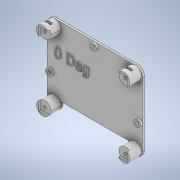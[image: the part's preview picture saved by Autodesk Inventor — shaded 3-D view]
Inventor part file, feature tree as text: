
AUTODESK INVENTOR PART (.ipt)
format: ipt  version: 2020.3 (Build 243373000, 373)  size: 1,038,336 bytes
history: native  units: mm
features: other x10, plane x8, sketch x8, extrude x6, projected_geometry x4, mirror x2, hole x1
ambient origin geometry x8: Origin, YZ Plane, XZ Plane, XY Plane, X Axis, Y Axis, Z Axis, Center Point
bodies: Volumenkörper2 (feature_tree), Volumenkörper1 (feature_tree)
feature tree (39):
  other  "Querschnitt1"
  other  "Querschnitt2"
  extrude  "Extrusion0"  Depth=31.5mm
  extrude  "Extrusion0.1"  Depth=31.5mm
  other  "Arbeitsachse1"
  plane  "Arbeitsebene1"
  sketch  "Skizze2.0"  dims[d0=2.0mm]
  plane  "Arbeitsebene7"
  sketch  "Skizze2.1"  dims[d9=3.5mm d10=31.5mm]
  other  "Arbeitspunkt1"
  other  "Arbeitsachse2"
  other  "Arbeitsachse3"
  plane  "Arbeitsebene2"
  sketch  "Skizze2.2"  dims[d16=3.2mm d17=3.2mm]
  extrude  "Extrusion2.0"  Depth=76.5mm
  plane  "Arbeitsebene4"
  plane  "Arbeitsebene5"
  hole  "Bohrung1"  [1 undecoded]
  extrude  "Extrusion2.1"  Depth=3.2mm
  extrude  "Extrusion6"  Depth=3.2mm
  plane  "Arbeitsebene3"
  extrude  "Extrusion2"  Depth=1.0mm
  mirror  "Spiegeln1"
  other  "Arbeitsachse4"
  other  "Arbeitsachse5"
  plane  "Arbeitsebene8"
  mirror  "Spiegeln2"
  other  "Prägen1"
  sketch  "Skizze1"  dims[d11=93.5mm d12=76.5mm]
  sketch  "Skizze3"  dims[d18=3.2mm d19=3.2mm]
  sketch  "Skizze4"  dims[d20=11.0mm d21=10.0mm d22=0.0mm d23=0.0mm d25=5.6mm d26=0.2mm d27=3.0mm d28=20.0mm d29=2.2mm d30=0.0mm d31=7.5mm d32=57.0mm d33=10.0mm d34=82.0mm d35=1.0mm d36=0.0mm d37=30.0mm d38=30.0mm d39=30.0mm d40=30.0mm d41=40.0mm d42=0.0mm d44=0.5mm d45=2.0mm d46=-33.0mm d47=20.0mm d50=75.2mm d51=90.2mm d52=7.0mm d53=12.0mm d54=0.0mm d55=2.0mm d58=13.0mm d59=13.0mm d60=10.0mm d61=0.0mm d62=82.0mm d63=67.0mm d72=82.0mm d73=67.0mm d75=82.0mm d76=2.0mm d77=0.0mm d78=14.0mm d81=0.0mm d82=67.0mm d83=0.5mm d84=2.0mm d85=40.75mm d86=20.0mm d87=6.5mm d89=67.0mm]
  sketch  "Skizze00"  dims[d1=4.0mm d2=6.0mm d3=4.0mm d4=2.0mm d5=90.0deg d6=8.0mm d7=20.594885mm d8=31.5mm]
  sketch  "Skizze01"  dims[d13=48.5mm d15=3.0mm]
  projected_geometry  "Projizierte Kontur4"
  projected_geometry  "Projizierte Kontur5"
  projected_geometry  "Projizierte Kontur6"
  projected_geometry  "Projizierte Kontur7"
  plane  "Arbeitsebene0"
  other  "Arbeitspunkt2"
note: 1 required parameter value undecoded (feature->parameter linkage not recoverable at this tier; creation-order binding heuristic only, values carry confidence <= 0.55)
